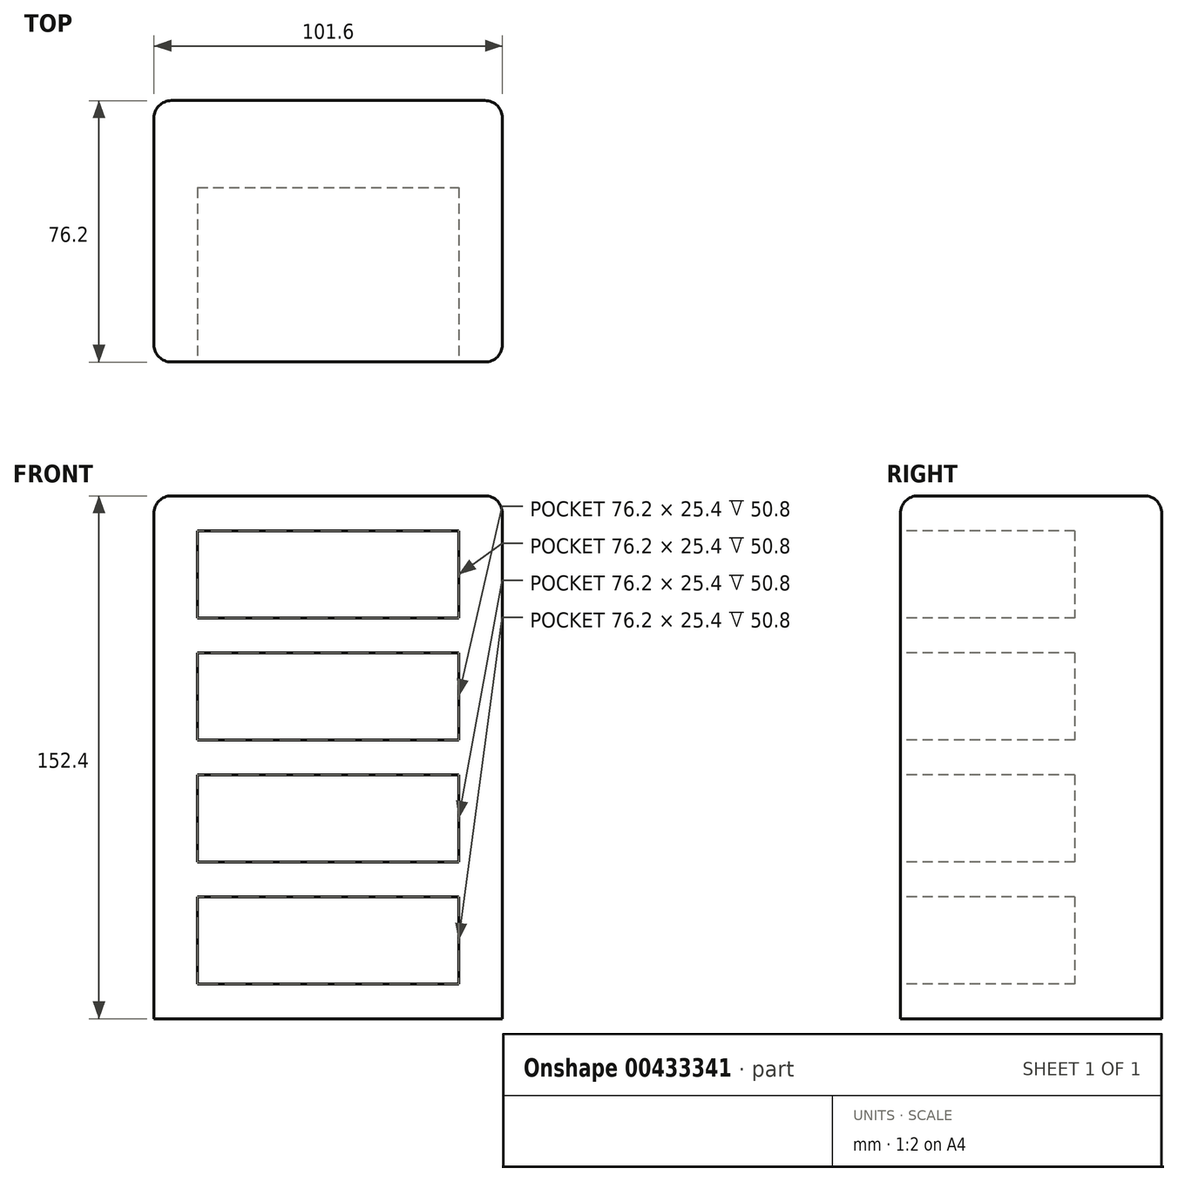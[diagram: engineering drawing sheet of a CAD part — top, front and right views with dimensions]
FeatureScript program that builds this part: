
annotation { "Feature Type Name" : "Feature", "Feature Type Description" : "" }
export const myFeature = defineFeature(function(context is Context, id is Id, definition is map)
    precondition{}
    {
        {
            var Q0;
            Q0=qCreatedBy(makeId("Top.planeOp"),FACE);
            var sketch = newSketch(context, id + "F0", { "sketchPlane" : qUnion([Q0])});
            skLineSegment(sketch, "E0.bottom", {"start": v(-50.25, 37.63) * mm, "end": v(51.35, 37.63) * mm});
            skLineSegment(sketch, "E0.top", {"start": v(-50.25, -38.57) * mm, "end": v(51.35, -38.57) * mm});
            skLineSegment(sketch, "E0.left", {"start": v(-50.25, 37.63) * mm, "end": v(-50.25, -38.57) * mm});
            skLineSegment(sketch, "E0.right", {"start": v(51.35, 37.63) * mm, "end": v(51.35, -38.57) * mm});
            skSolve(sketch);
        }
        {
            var Q0;
            Q0=makeQuery(id+"F0.imprint","IMPRINT",FACE,{"disambiguationData":[TD([[makeQuery(id+"F0.imprint","IMPRINT",EDGE,{"derivedFrom":sQuery(id+"F0.wireOp",EDGE,"E0.bottom")}),-1.0]])]});
            extrude(context, id + "F1", {"entities" : qUnion([Q0]), "depth" : 152.4 * mm});
        }
        {
            var Q0;
            Q0=makeQuery(id+"F1.opExtrude","SWEPT_FACE",FACE,{"disambiguationData":[OSD([sQuery(id+"F0.wireOp",EDGE,"E0.top")])]});
            var sketch = newSketch(context, id + "F2", { "sketchPlane" : qUnion([Q0])});
            skLineSegment(sketch, "E1.bottom", {"start": v(-37.55, 142.24) * mm, "end": v(38.65, 142.24) * mm});
            skLineSegment(sketch, "E1.top", {"start": v(-37.55, 116.84) * mm, "end": v(38.65, 116.84) * mm});
            skLineSegment(sketch, "E1.left", {"start": v(-37.55, 142.24) * mm, "end": v(-37.55, 116.84) * mm});
            skLineSegment(sketch, "E1.right", {"start": v(38.65, 142.24) * mm, "end": v(38.65, 116.84) * mm});
            skLineSegment(sketch, "E2.0.1.0", {"start": v(-37.55, 106.68) * mm, "end": v(38.65, 106.68) * mm});
            skLineSegment(sketch, "E2.0.1.1", {"start": v(-37.55, 106.68) * mm, "end": v(-37.55, 81.28) * mm});
            skLineSegment(sketch, "E2.0.1.2", {"start": v(-37.55, 81.28) * mm, "end": v(38.65, 81.28) * mm});
            skLineSegment(sketch, "E2.0.1.3", {"start": v(38.65, 106.68) * mm, "end": v(38.65, 81.28) * mm});
            skLineSegment(sketch, "E2.0.2.0", {"start": v(-37.55, 71.12) * mm, "end": v(38.65, 71.12) * mm});
            skLineSegment(sketch, "E2.0.2.1", {"start": v(-37.55, 71.12) * mm, "end": v(-37.55, 45.72) * mm});
            skLineSegment(sketch, "E2.0.2.2", {"start": v(-37.55, 45.72) * mm, "end": v(38.65, 45.72) * mm});
            skLineSegment(sketch, "E2.0.2.3", {"start": v(38.65, 71.12) * mm, "end": v(38.65, 45.72) * mm});
            skLineSegment(sketch, "E2.0.3.0", {"start": v(-37.55, 35.56) * mm, "end": v(38.65, 35.56) * mm});
            skLineSegment(sketch, "E2.0.3.1", {"start": v(-37.55, 35.56) * mm, "end": v(-37.55, 10.16) * mm});
            skLineSegment(sketch, "E2.0.3.2", {"start": v(-37.55, 10.16) * mm, "end": v(38.65, 10.16) * mm});
            skLineSegment(sketch, "E2.0.3.3", {"start": v(38.65, 35.56) * mm, "end": v(38.65, 10.16) * mm});
            skLineSegment(sketch, "E2.direction1", {"start": v(-37.55, 142.24) * mm, "end": v(-12.15, 142.24) * mm, "construction": true});
            skLineSegment(sketch, "E2.direction2", {"start": v(-37.55, 142.24) * mm, "end": v(-37.55, 106.68) * mm, "construction": true});
            skSolve(sketch);
        }
        {
            var Q0;
            Q0=makeQuery(id+"F2.imprint","IMPRINT",FACE,{"disambiguationData":[TD([[makeQuery(id+"F2.imprint","IMPRINT",EDGE,{"derivedFrom":sQuery(id+"F2.wireOp",EDGE,"E2.0.1.0")}),-1.0]])]});
            var Q1;
            Q1=makeQuery(id+"F2.imprint","IMPRINT",FACE,{"disambiguationData":[TD([[makeQuery(id+"F2.imprint","IMPRINT",EDGE,{"derivedFrom":sQuery(id+"F2.wireOp",EDGE,"E1.bottom")}),-1.0]])]});
            var Q2;
            Q2=makeQuery(id+"F2.imprint","IMPRINT",FACE,{"disambiguationData":[TD([[makeQuery(id+"F2.imprint","IMPRINT",EDGE,{"derivedFrom":sQuery(id+"F2.wireOp",EDGE,"E2.0.2.0")}),-1.0]])]});
            var Q3;
            Q3=makeQuery(id+"F2.imprint","IMPRINT",FACE,{"disambiguationData":[TD([[makeQuery(id+"F2.imprint","IMPRINT",EDGE,{"derivedFrom":sQuery(id+"F2.wireOp",EDGE,"E2.0.3.0")}),-1.0]])]});
            extrude(context, id + "F3", {"entities" : qUnion([Q0, Q1, Q2, Q3]), "operationType" : NewBodyOperationType.REMOVE, "oppositeDirection" : true, "depth" : 50.8 * mm});
        }
        {
            var Q0;
            Q0=makeQuery(id+"F1.opExtrude","CAP_EDGE",EDGE,{"disambiguationData":[OSD([sQuery(id+"F0.wireOp",EDGE,"E0.right")])],"isStart":false});
            var Q1;
            Q1=makeQuery(id+"F1.opExtrude","CAP_EDGE",EDGE,{"disambiguationData":[OSD([sQuery(id+"F0.wireOp",EDGE,"E0.left")])],"isStart":false});
            var Q2;
            Q2=makeQuery(id+"F1.opExtrude","CAP_EDGE",EDGE,{"disambiguationData":[OSD([sQuery(id+"F0.wireOp",EDGE,"E0.top")])],"isStart":false});
            var Q3;
            Q3=makeQuery(id+"F1.opExtrude","CAP_EDGE",EDGE,{"disambiguationData":[OSD([sQuery(id+"F0.wireOp",EDGE,"E0.bottom")])],"isStart":false});
            var Q4;
            Q4=makeQuery(id+"F1.opExtrude","SWEPT_EDGE",EDGE,{"disambiguationData":[OSD([sQuery(id+"F0.wireOp",EDGE,"E0.top"),sQuery(id+"F0.wireOp",EDGE,"E0.right")])]});
            var Q5;
            Q5=makeQuery(id+"F1.opExtrude","SWEPT_EDGE",EDGE,{"disambiguationData":[OSD([sQuery(id+"F0.wireOp",EDGE,"E0.top"),sQuery(id+"F0.wireOp",EDGE,"E0.left")])]});
            var Q6;
            Q6=makeQuery(id+"F1.opExtrude","SWEPT_EDGE",EDGE,{"disambiguationData":[OSD([sQuery(id+"F0.wireOp",EDGE,"E0.bottom"),sQuery(id+"F0.wireOp",EDGE,"E0.right")])]});
            var Q7;
            Q7=makeQuery(id+"F1.opExtrude","SWEPT_EDGE",EDGE,{"disambiguationData":[OSD([sQuery(id+"F0.wireOp",EDGE,"E0.bottom"),sQuery(id+"F0.wireOp",EDGE,"E0.left")])]});
            fillet(context, id + "F4", {"entities" : qUnion([Q0, Q1, Q2, Q3, Q4, Q5, Q6, Q7]), "radius" : 5.08 * mm, "tangentPropagation" : true, "allowEdgeOverflow" : false});
        }
    });
